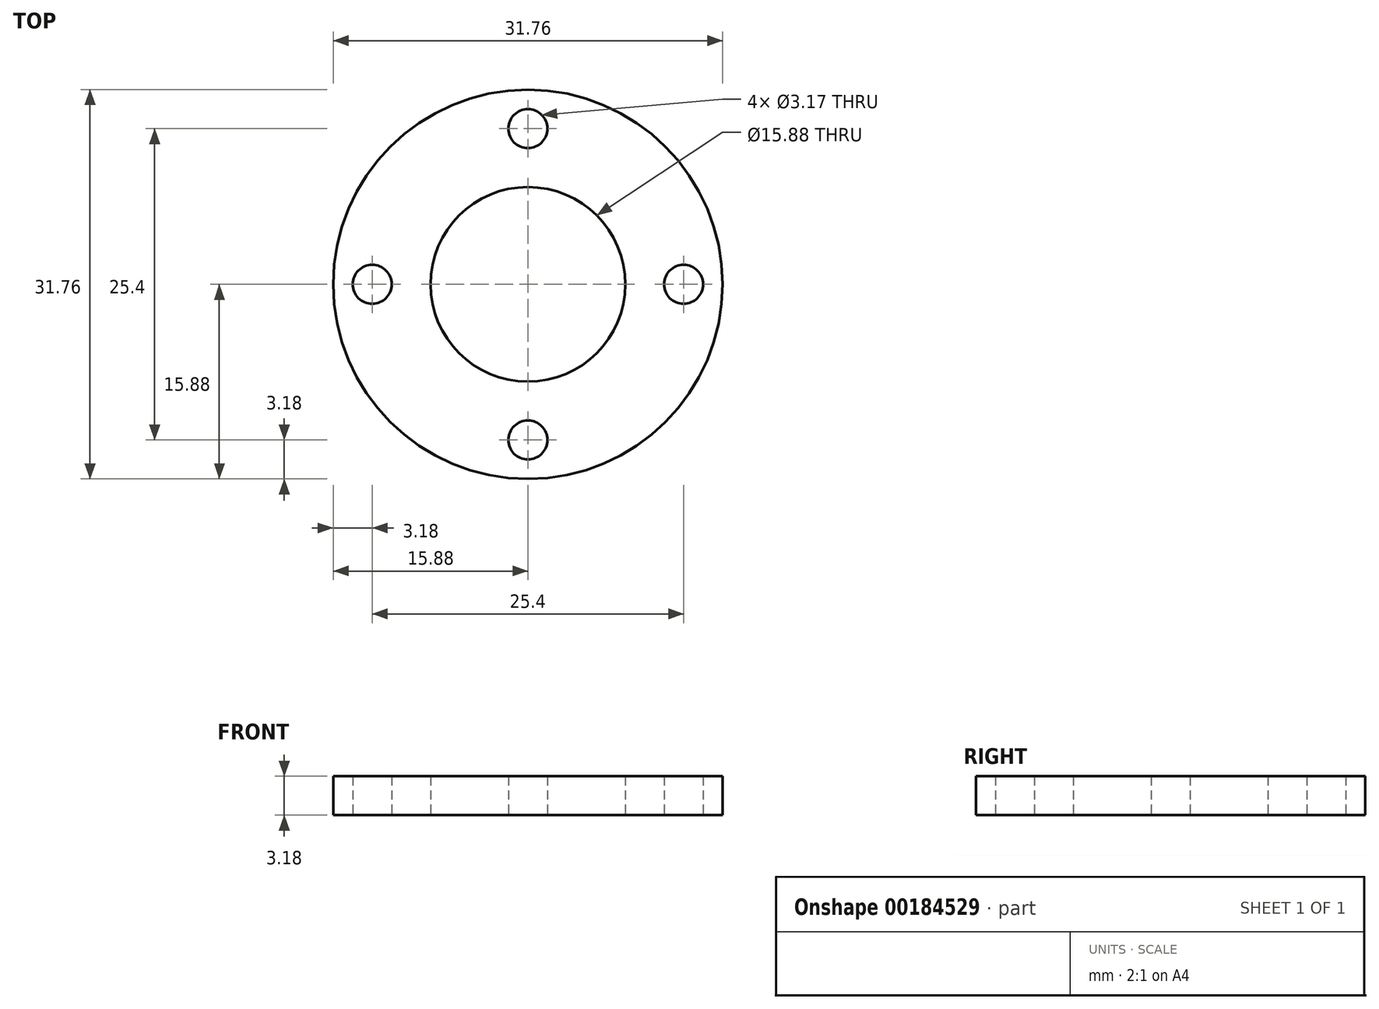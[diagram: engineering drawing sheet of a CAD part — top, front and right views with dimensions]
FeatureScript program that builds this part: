
annotation { "Feature Type Name" : "Feature", "Feature Type Description" : "" }
export const myFeature = defineFeature(function(context is Context, id is Id, definition is map)
    precondition{}
    {
        {
            var Q0;
            Q0=qCreatedBy(makeId("Top.planeOp"),FACE);
            var sketch = newSketch(context, id + "F0", { "sketchPlane" : qUnion([Q0])});
            skCircle(sketch, "E0", {"center": v(0, 0) * mm, "radius": 7.94 * mm});
            skCircle(sketch, "E1.0", {"center": v(0, 0) * mm, "radius": 15.88 * mm});
            skCircle(sketch, "E2", {"center": v(-12.7, 0) * mm, "radius": 1.59 * mm});
            skCircle(sketch, "E3", {"center": v(12.7, 0) * mm, "radius": 1.59 * mm});
            skCircle(sketch, "E4", {"center": v(0, 12.7) * mm, "radius": 1.59 * mm});
            skCircle(sketch, "E5", {"center": v(0, -12.7) * mm, "radius": 1.59 * mm});
            skSolve(sketch);
        }
        {
            var Q0;
            Q0=makeQuery(id+"F0.imprint","IMPRINT",FACE,{"disambiguationData":[TD([[makeQuery(id+"F0.imprint","IMPRINT",EDGE,{"derivedFrom":sQuery(id+"F0.wireOp",EDGE,"E0")}),-1.0]])]});
            extrude(context, id + "F1", {"entities" : qUnion([Q0]), "endBound" : BoundingType.SYMMETRIC, "depth" : 3.17 * mm});
        }
    });
